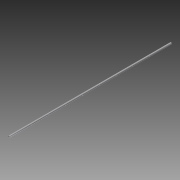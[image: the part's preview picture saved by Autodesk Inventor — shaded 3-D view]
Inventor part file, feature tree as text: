
AUTODESK INVENTOR PART (.ipt)
format: ipt  version: 2013 (Build 170138000, 138)  size: 125,440 bytes
history: native  units: in
note: dims shown in document units (in); Inventor stores cm internally (conversion verified against a paired STEP export)
features: sketch x2, extrude x1, plane x1, hole x1
ambient origin geometry x8: Origin, YZ Plane, XZ Plane, XY Plane, X Axis, Y Axis, Z Axis, Center Point
bodies: Solid1 (feature_tree)
feature tree (5):
  extrude  "Extrusion1"  Depth=0.091in
  plane  "Work Plane1"
  hole  "Hole1"  [1 undecoded]
  sketch  "Sketch1"  dims[d0=0.675in d2=0.091in]
  sketch  "Sketch2"  dims[d3=62.5in d4=0.0in d5=8.5in d6=15.0in d7=21.5in d8=28.0in d9=0.2in d10=0.75in d11=0.375in d12=0.25in d13=0.5635in d14=1.0in d15=0.8108in d16=34.5in d17=41.0in d18=47.5in d19=54.0in]
note: 1 required parameter value undecoded (feature->parameter linkage not recoverable at this tier; creation-order binding heuristic only, values carry confidence <= 0.55)
